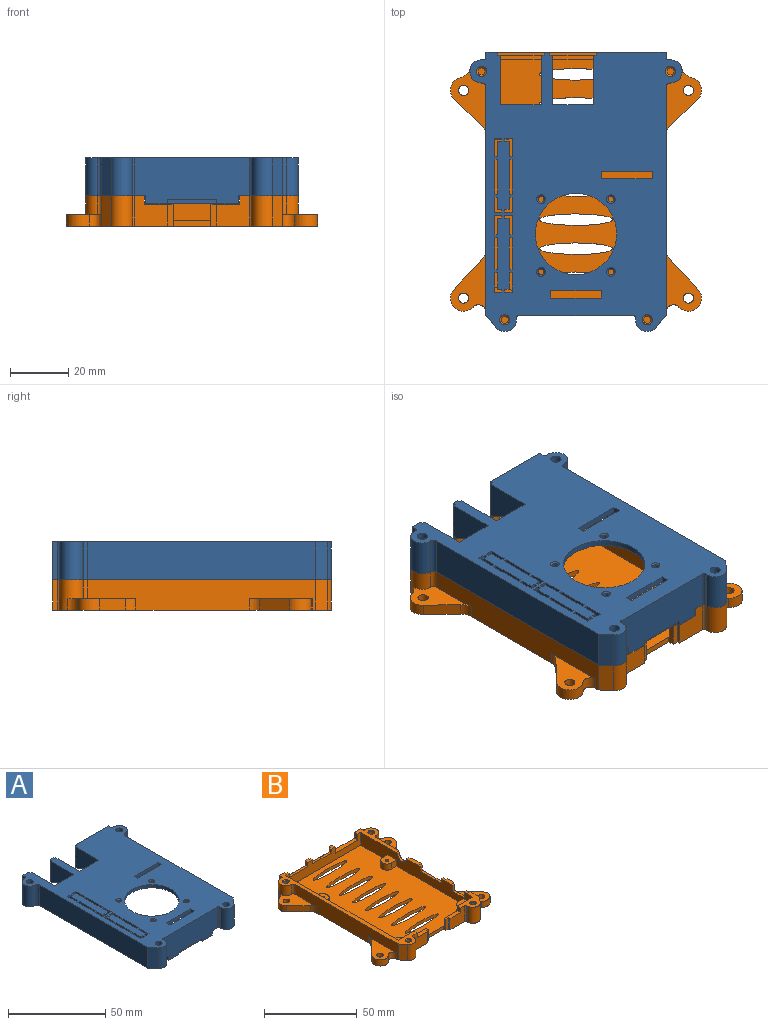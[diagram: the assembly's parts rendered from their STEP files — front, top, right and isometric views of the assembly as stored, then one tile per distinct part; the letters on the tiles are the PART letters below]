
ASSEMBLY  parts=2 mates=1
PART A: 159 faces, bbox 73x96x15.8 mm
  f0: plane 32x2.5mm, normal (0,0,-1), area 63mm2, adj f67,f68,f153,f154,f155,f156,f157
  f1: plane 96x20.5mm, normal (0,0,-1), area 322.4mm2, adj f67,f68,f69,f70,f71,f72,f73,f74
  f2: plane 30.5x10.5mm, normal (0,0,-1), area 109.1mm2, adj f3,f4,f65,f90,f91,f92,f93,f94
  f3: plane 78.5x13mm, normal (1,0,0), area 841.2mm2, adj f2,f5,f6,f52,f85,f89,f90,f140
  f4: plane 85.5x11mm, normal (-1,0,0), area 848.3mm2, adj f2,f5,f6,f7,f68,f85,f96,f136
  f5: plane 10.5x2.5mm, normal (0,0,-1), area 22.8mm2, adj f3,f4,f144,f146,f147,f150,f151,f152
  f6: plane 8.5x2.5mm, normal (0,0,-1), area 17.8mm2, adj f3,f4,f137,f139,f140,f143,f146,f148
  f7: plane 85.5x57mm, normal (0,0,-1), area 2695.7mm2, adj f4,f53,f59,f63,f64,f68,f69,f70
  f8: plane 12x1.2mm, normal (1,0,0), area 14.4mm2, adj f9,f10,f52,f134
  f9: plane 1.2x1mm, normal (0,-1,0), area 1.2mm2, adj f8,f52,f125,f134
  f10: plane 1.2x1mm, normal (0,1,0), area 1.2mm2, adj f8,f52,f125,f134
  f11: plane 1.2x1mm, normal (0,-1,0), area 1.2mm2, adj f13,f52,f123,f134
  f12: plane 1.2x1mm, normal (0,1,0), area 1.2mm2, adj f13,f52,f123,f134
  f13: plane 12x1.2mm, normal (-1,0,0), area 14.4mm2, adj f11,f12,f52,f134
  f14: plane 1.2x1mm, normal (-1,0,0), area 1.2mm2, adj f16,f52,f106,f134
  f15: plane 1.2x1mm, normal (0,-1,0), area 1.2mm2, adj f17,f52,f123,f134
  f16: plane 1.5x1.2mm, normal (0,-1,0), area 1.8mm2, adj f14,f17,f52,f134
  f17: plane 4.25x1.2mm, normal (-1,0,0), area 5.1mm2, adj f15,f16,f52,f134
  f18: plane 1.2x1mm, normal (0,-1,0), area 1.2mm2, adj f20,f52,f125,f134
  f19: plane 1.2x1mm, normal (1,0,0), area 1.2mm2, adj f21,f52,f106,f134
  f20: plane 4.25x1.2mm, normal (1,0,0), area 5.1mm2, adj f18,f21,f52,f134
  f21: plane 1.5x1.2mm, normal (0,-1,0), area 1.8mm2, adj f19,f20,f52,f134
  f22: plane 1.2x1mm, normal (1,0,0), area 1.2mm2, adj f23,f52,f107,f135
  f23: plane 1.5x1.2mm, normal (0,1,0), area 1.8mm2, adj f22,f24,f52,f135
  f24: plane 5.75x1.2mm, normal (1,0,0), area 6.9mm2, adj f23,f25,f52,f135
  f25: plane 1.2x1mm, normal (0,1,0), area 1.2mm2, adj f24,f52,f122,f135
  f26: plane 1.2x1mm, normal (0,1,0), area 1.2mm2, adj f27,f52,f120,f135
  f27: plane 5.75x1.2mm, normal (-1,0,0), area 6.9mm2, adj f26,f28,f52,f135
  f28: plane 1.5x1.2mm, normal (0,1,0), area 1.8mm2, adj f27,f29,f52,f135
  f29: plane 1.2x1mm, normal (-1,0,0), area 1.2mm2, adj f28,f52,f107,f135
  f30: plane 1.2x1mm, normal (0,-1,0), area 1.2mm2, adj f32,f52,f120,f135
  f31: plane 1.2x1mm, normal (0,1,0), area 1.2mm2, adj f32,f52,f120,f135
  f32: plane 11x1.2mm, normal (-1,0,0), area 13.2mm2, adj f30,f31,f52,f135
  f33: plane 1.2x1mm, normal (0,-1,0), area 1.2mm2, adj f34,f52,f122,f135
  f34: plane 11x1.2mm, normal (1,0,0), area 13.2mm2, adj f33,f35,f52,f135
  f35: plane 1.2x1mm, normal (0,1,0), area 1.2mm2, adj f34,f52,f122,f135
  f36: plane 1.2x1mm, normal (-1,0,0), area 1.2mm2, adj f37,f52,f121,f135
  f37: plane 1.5x1.2mm, normal (0,-1,0), area 1.8mm2, adj f36,f38,f52,f135
  f38: plane 5.75x1.2mm, normal (-1,0,0), area 6.9mm2, adj f37,f39,f52,f135
  f39: plane 1.2x1mm, normal (0,-1,0), area 1.2mm2, adj f38,f52,f120,f135
  f40: plane 1.2x1mm, normal (0,-1,0), area 1.2mm2, adj f42,f52,f122,f135
  f41: plane 1.2x1mm, normal (1,0,0), area 1.2mm2, adj f43,f52,f121,f135
  f42: plane 5.75x1.2mm, normal (1,0,0), area 6.9mm2, adj f40,f43,f52,f135
  f43: plane 1.5x1.2mm, normal (0,-1,0), area 1.8mm2, adj f41,f42,f52,f135
  f44: plane 1.2x1mm, normal (0,1,0), area 1.2mm2, adj f45,f52,f123,f134
  f45: plane 5.25x1.2mm, normal (-1,0,0), area 6.3mm2, adj f44,f46,f52,f134
  f46: plane 1.5x1.2mm, normal (0,1,0), area 1.8mm2, adj f45,f47,f52,f134
  f47: plane 1.2x1mm, normal (-1,0,0), area 1.2mm2, adj f46,f52,f124,f134
  f48: plane 1.2x1mm, normal (1,0,0), area 1.2mm2, adj f49,f52,f124,f134
  f49: plane 1.5x1.2mm, normal (0,1,0), area 1.8mm2, adj f48,f50,f52,f134
  f50: plane 5.25x1.2mm, normal (1,0,0), area 6.3mm2, adj f49,f51,f52,f134
  f51: plane 1.2x1mm, normal (0,1,0), area 1.2mm2, adj f50,f52,f125,f134
  f52: plane 96x73mm, normal (0,0,1), area 4382.9mm2, adj f3,f8,f9,f10,f11,f12,f13,f14
  f53: plane 32x13mm, normal (1,0,0), area 186.2mm2, adj f7,f52,f54,f60,f97,f99,f103,f104
  f54: plane 13x1mm, normal (0,1,0), area 13mm2, adj f52,f53,f55,f60
  f55: plane 13x1mm, normal (1,0,0), area 13mm2, adj f52,f54,f56,f60
  f56: plane 13x2mm, normal (0,1,0), area 26mm2, adj f52,f55,f57,f60
  f57: plane 13x1mm, normal (-1,0,0), area 13mm2, adj f52,f56,f58,f60
  f58: plane 13x1mm, normal (0,1,0), area 13mm2, adj f52,f57,f59,f60
  f59: plane 24x13mm, normal (-1,0,0), area 174.3mm2, adj f7,f52,f58,f60,f98,f99
  f60: plane 4x2.5mm, normal (0,0,-1), area 8mm2, adj f53,f54,f55,f56,f57,f58,f59,f99
  f61: plane 13x1mm, normal (-1,0,0), area 13mm2, adj f52,f62,f65,f66
  f62: plane 13x1mm, normal (0,1,0), area 13mm2, adj f52,f61,f63,f66
  f63: plane 32x13mm, normal (-1,0,0), area 186.3mm2, adj f7,f52,f62,f66,f97,f100,f103,f104
  f64: plane 25x11.8mm, normal (1,0,0), area 169.6mm2, adj f7,f65,f66,f100,f101,f102
  f65: plane 24x13mm, normal (0,1,0), area 111.4mm2, adj f2,f52,f61,f64,f66,f94,f95,f102
  f66: plane 3x2.5mm, normal (0,0,-1), area 6.5mm2, adj f61,f62,f63,f64,f65,f100
  f67: plane 39.5x15.8mm, normal (0,-1,0), area 577.6mm2, adj f0,f1,f52,f84,f85,f86,f153,f154
  f68: plane 57x13.8mm, normal (0,1,0), area 716.6mm2, adj f0,f1,f4,f7,f69,f85,f153,f154
  f69: plane 85.5x11mm, normal (1,0,0), area 940.5mm2, adj f1,f7,f68,f70
  f70: plane 11x2.5mm, normal (0,-1,0), area 27.5mm2, adj f1,f7,f69,f71
  f71: plane 17x13mm, normal (1,0,0), area 50.5mm2, adj f1,f7,f52,f70,f72,f98
  f72: plane 13x1mm, normal (0,1,0), area 13mm2, adj f1,f52,f71,f73
  f73: plane 13x1mm, normal (1,0,0), area 13mm2, adj f1,f52,f72,f74
  f74: plane 13x4mm, normal (0,1,0), area 52mm2, adj f1,f52,f73,f75
  f75: plane 13x1.75mm, normal (-1,0,0), area 22.8mm2, adj f1,f52,f74,f76
  f76: cylinder r=0.75mm len=13mm, axis (0,0,-1), area 15.3mm2, adj f1,f52,f75,f77
  f77: plane 13x0.75mm, normal (0,1,0), area 9.7mm2, adj f1,f52,f76,f78
  f78: cylinder r=4mm len=13mm, axis (0,0,-1), area 163.4mm2, adj f1,f52,f77,f79
  f79: cylinder r=1.5mm len=13mm, axis (0,0,-1), area 30.6mm2, adj f1,f52,f78,f80
  f80: plane 78.5x13mm, normal (-1,0,0), area 1020.5mm2, adj f1,f52,f79,f81
  f81: plane 13x4.08mm, normal (-0.76,-0.64,0), area 69.4mm2, adj f1,f52,f80,f82
  f82: cylinder r=4mm len=13mm, axis (0,0,-1), area 126.9mm2, adj f1,f52,f81,f83
  f83: plane 13x0.75mm, normal (1,0,0), area 9.7mm2, adj f1,f52,f82,f84
  f84: cylinder r=0.75mm len=13mm, axis (0,0,-1), area 15.3mm2, adj f1,f52,f67,f83
  f85: plane 15x14.5mm, normal (0,0,-1), area 83.8mm2, adj f3,f4,f67,f68,f86,f87,f88,f89
  f86: cylinder r=0.75mm len=13mm, axis (0,0,-1), area 15.3mm2, adj f52,f67,f85,f87
  f87: plane 13x0.75mm, normal (-1,0,0), area 9.7mm2, adj f52,f85,f86,f88
  f88: cylinder r=4mm len=13mm, axis (0,0,-1), area 126.9mm2, adj f52,f85,f87,f89
  f89: plane 13x4.08mm, normal (0.76,-0.64,0), area 69.4mm2, adj f3,f52,f85,f88
  f90: cylinder r=1.5mm len=13mm, axis (0,0,-1), area 30.6mm2, adj f2,f3,f52,f91
  f91: cylinder r=4mm len=13mm, axis (0,0,-1), area 163.4mm2, adj f2,f52,f90,f92
  f92: plane 13x0.75mm, normal (0,1,0), area 9.8mm2, adj f2,f52,f91,f93
  f93: cylinder r=0.75mm len=13mm, axis (0,0,-1), area 15.3mm2, adj f2,f52,f92,f94
  f94: plane 13x1.75mm, normal (1,0,0), area 22.8mm2, adj f2,f52,f65,f93
  f95: plane 23x11.8mm, normal (-1,0,0), area 45.9mm2, adj f2,f7,f65,f96,f101,f102
  f96: plane 11x2.5mm, normal (0,-1,0), area 27.5mm2, adj f2,f4,f7,f95
  f97: plane 14x1.2mm, normal (0,1,0), area 16.8mm2, adj f52,f53,f63,f104
  f98: plane 14x2mm, normal (0,1,0), area 28mm2, adj f7,f52,f59,f71
  f99: plane 22.5x11mm, normal (0,-0.44,-0.9), area 100.2mm2, adj f7,f53,f59,f60
  f100: plane 22.5x11mm, normal (0,-0.44,-0.9), area 75.1mm2, adj f7,f63,f64,f66
  f101: plane 17x0.8mm, normal (0,1,0), area 13.6mm2, adj f7,f64,f95,f102
  f102: plane 23x17mm, normal (0,0,-1), area 391mm2, adj f64,f65,f95,f101
  f103: plane 14x0.8mm, normal (0,1,0), area 11.2mm2, adj f7,f53,f63,f104
  f104: plane 15x14mm, normal (0,0,-1), area 210mm2, adj f53,f63,f97,f103
  f105: cylinder r=14mm len=28mm, axis (0,0,1), area 175.9mm2, adj f7,f52
  f106: plane 6x2mm, normal (0,1,0), area 10.8mm2, adj f7,f14,f19,f52,f123,f125,f134
  f107: plane 6x2mm, normal (0,-1,0), area 10.8mm2, adj f7,f22,f29,f52,f120,f122,f135
  f108: cylinder r=1mm len=2mm, axis (0,0,1), area 9.4mm2, adj f7,f127
  f109: plane 2.5x2mm, normal (1,0,0), area 5mm2, adj f7,f52,f110,f111
  f110: plane 17.5x2mm, normal (0,-1,0), area 35mm2, adj f7,f52,f109,f112
  f111: plane 17.5x2mm, normal (0,1,0), area 35mm2, adj f7,f52,f109,f112
  f112: plane 2.5x2mm, normal (-1,0,0), area 5mm2, adj f7,f52,f110,f111
  f113: cylinder r=1mm len=2mm, axis (0,0,1), area 9.4mm2, adj f7,f126
  f114: cylinder r=1mm len=2mm, axis (0,0,1), area 9.4mm2, adj f7,f129
  f115: cylinder r=1mm len=2mm, axis (0,0,1), area 9.4mm2, adj f7,f128
  f116: plane 2.5x2mm, normal (1,0,0), area 5mm2, adj f7,f52,f117,f118
  f117: plane 17.5x2mm, normal (0,-1,0), area 35mm2, adj f7,f52,f116,f119
  f118: plane 17.5x2mm, normal (0,1,0), area 35mm2, adj f7,f52,f116,f119
  f119: plane 2.5x2mm, normal (-1,0,0), area 5mm2, adj f7,f52,f117,f118
  f120: plane 26.5x2mm, normal (1,0,0), area 50.6mm2, adj f7,f26,f30,f31,f39,f52,f107,f121
  f121: plane 6x2mm, normal (0,1,0), area 10.8mm2, adj f7,f36,f41,f52,f120,f122,f135
  f122: plane 26.5x2mm, normal (-1,0,0), area 50.6mm2, adj f7,f25,f33,f35,f40,f52,f107,f121
  f123: plane 25.5x2mm, normal (1,0,0), area 48.6mm2, adj f7,f11,f12,f15,f44,f52,f106,f124
  f124: plane 6x2mm, normal (0,-1,0), area 10.8mm2, adj f7,f47,f48,f52,f123,f125,f134
  f125: plane 25.5x2mm, normal (-1,0,0), area 48.6mm2, adj f7,f9,f10,f18,f51,f52,f106,f124
  f126: cone r=1mm half-angle=45deg, axis (0,0,1), area 5.6mm2, adj f52,f113
  f127: cone r=1mm half-angle=45deg, axis (0,0,1), area 5.6mm2, adj f52,f108
  f128: cone r=1mm half-angle=45deg, axis (0,0,1), area 5.6mm2, adj f52,f115
  f129: cone r=1mm half-angle=45deg, axis (0,0,1), area 5.6mm2, adj f52,f114
  f130: cylinder r=1.75mm len=13mm, axis (0,0,1), area 142.9mm2, adj f1,f52
  f131: cylinder r=1.75mm len=13mm, axis (0,0,1), area 142.9mm2, adj f52,f85
  f132: cylinder r=1.75mm len=13mm, axis (0,0,1), area 142.9mm2, adj f2,f52
  f133: cylinder r=1.75mm len=13mm, axis (0,0,1), area 142.9mm2, adj f1,f52
  f134: plane 25.5x6mm, normal (0,0,-1), area 100mm2, adj f8,f9,f10,f11,f12,f13,f14,f15
  f135: plane 26.5x6mm, normal (0,0,-1), area 104mm2, adj f22,f23,f24,f25,f26,f27,f28,f29
  f136: plane 1.5x1mm, normal (0,1,0), area 1.5mm2, adj f4,f85,f138,f139
  f137: plane 1.5x1mm, normal (0,-1,0), area 1.5mm2, adj f4,f6,f138,f139
  f138: plane 9x1.5mm, normal (0,0,-1), area 13.5mm2, adj f4,f136,f137,f139
  f139: plane 12x2.5mm, normal (1,0,0), area 21mm2, adj f6,f85,f136,f137,f138,f140,f141,f142
  f140: plane 2.5x1mm, normal (0,-1,0), area 2.5mm2, adj f3,f6,f139,f142
  f141: plane 2.5x1mm, normal (0,1,0), area 2.5mm2, adj f3,f85,f139,f142
  f142: plane 12x1mm, normal (0,0,-1), area 12mm2, adj f3,f139,f140,f141
  f143: plane 4x1.5mm, normal (0,1,0), area 6mm2, adj f4,f6,f145,f146
  f144: plane 4x1.5mm, normal (0,-1,0), area 6mm2, adj f4,f5,f145,f146
  f145: plane 16x1.5mm, normal (0,0,-1), area 24mm2, adj f4,f143,f144,f146
  f146: plane 20x5.5mm, normal (1,0,0), area 46mm2, adj f5,f6,f143,f144,f145,f147,f148,f149
  f147: plane 5.5x1mm, normal (0,-1,0), area 5.5mm2, adj f3,f5,f146,f149
  f148: plane 5.5x1mm, normal (0,1,0), area 5.5mm2, adj f3,f6,f146,f149
  f149: plane 20x1mm, normal (0,0,-1), area 20mm2, adj f3,f146,f147,f148
  f150: cylinder r=3.5mm len=7mm, axis (1,0,0), area 16.5mm2, adj f2,f4,f5,f152
  f151: cylinder r=5mm len=10mm, axis (1,0,0), area 15.7mm2, adj f2,f3,f5,f152
  f152: plane 10x5mm, normal (1,0,0), area 20mm2, adj f2,f5,f150,f151
  f153: plane 2.8x2.5mm, normal (-1,0,0), area 7mm2, adj f0,f1,f67,f68
  f154: plane 2.8x2.5mm, normal (1,0,0), area 7mm2, adj f0,f67,f68,f85
  f155: plane 1.5x1mm, normal (1,0,0), area 1.5mm2, adj f0,f67,f156,f158
  f156: plane 17x1.5mm, normal (0,-1,0), area 25.5mm2, adj f0,f155,f157,f158
  f157: plane 1.5x1mm, normal (-1,0,0), area 1.5mm2, adj f0,f67,f156,f158
  f158: plane 17x1mm, normal (0,0,-1), area 17mm2, adj f67,f155,f156,f157
PART B: 150 faces, bbox 86.4x96x10.5 mm
  f0: cylinder r=1.25mm len=7mm, axis (0,0,-1), area 55mm2, adj f145,f146
  f1: cylinder r=1.25mm len=7mm, axis (0,0,-1), area 55mm2, adj f144,f147
  f2: cylinder r=1.25mm len=7mm, axis (0,0,-1), area 55mm2, adj f143,f148
  f3: cylinder r=1.25mm len=7mm, axis (0,0,-1), area 55mm2, adj f142,f149
  f4: plane 78.5x10.5mm, normal (1,0,0), area 466.2mm2, adj f10,f11,f21,f22,f23,f68,f69,f70
  f5: plane 78.5x10.5mm, normal (-1,0,0), area 671.5mm2, adj f10,f14,f97,f105,f117,f121,f122,f125
  f6: plane 11.25x10.5mm, normal (0,-1,0), area 94.1mm2, adj f10,f11,f88,f89,f92,f99
  f7: plane 11.25x10.5mm, normal (0,-1,0), area 94.1mm2, adj f10,f14,f86,f87,f91,f94
  f8: plane 7.5x2mm, normal (-1,0,0), area 12.2mm2, adj f10,f33,f35,f39,f88,f93
  f9: plane 7.5x2mm, normal (1,0,0), area 12.2mm2, adj f10,f12,f35,f39,f86,f90
  f10: plane 96x86.39mm, normal (0,0,-1), area 5621.8mm2, adj f4,f5,f6,f7,f8,f9,f24,f35
  f11: plane 14.5x14.5mm, normal (0,0,1), area 82.6mm2, adj f4,f6,f28,f32,f33,f68,f71,f89
  f12: plane 22x8.5mm, normal (0,1,0), area 127mm2, adj f9,f14,f34,f39,f47,f50,f86,f87
  f13: plane 4x2.5mm, normal (0,0,1), area 8mm2, adj f15,f20,f36,f38,f80,f81,f82,f85
  f14: plane 96x20mm, normal (0,0,1), area 321.2mm2, adj f5,f7,f12,f17,f34,f36,f37,f38
  f15: plane 2.5x1.5mm, normal (-1,0,0), area 3.8mm2, adj f13,f16,f38,f85
  f16: plane 14x1.5mm, normal (0,0,1), area 21mm2, adj f15,f17,f38,f85
  f17: plane 2.5x1.5mm, normal (1,0,0), area 3.8mm2, adj f14,f16,f38,f85
  f18: plane 2.5x1.5mm, normal (-1,0,0), area 3.8mm2, adj f19,f31,f38,f81
  f19: plane 14x1.5mm, normal (0,0,1), area 21mm2, adj f18,f20,f38,f81
  f20: plane 2.5x1.5mm, normal (1,0,0), area 3.8mm2, adj f13,f19,f38,f81
  f21: plane 8.5x2.5mm, normal (0,0,1), area 17.8mm2, adj f4,f25,f30,f32,f70,f71,f72,f75
  f22: plane 10.5x2.5mm, normal (0,0,1), area 22.8mm2, adj f4,f27,f32,f64,f74,f75,f76,f77
  f23: plane 30.5x10.5mm, normal (0,0,1), area 109.1mm2, adj f4,f24,f32,f36,f38,f64,f65,f76
  f24: plane 10.5x1.75mm, normal (1,0,0), area 18.4mm2, adj f10,f23,f36,f108
  f25: plane 3x1.5mm, normal (0,1,0), area 4.5mm2, adj f21,f26,f32,f75
  f26: plane 16x1.5mm, normal (0,0,1), area 24mm2, adj f25,f27,f32,f75
  f27: plane 3x1.5mm, normal (0,-1,0), area 4.5mm2, adj f22,f26,f32,f75
  f28: plane 4x1.5mm, normal (0,1,0), area 6mm2, adj f11,f29,f32,f71
  f29: plane 9x1.5mm, normal (0,0,1), area 13.5mm2, adj f28,f30,f32,f71
  f30: plane 4x1.5mm, normal (0,-1,0), area 6mm2, adj f21,f29,f32,f71
  f31: plane 3x2.5mm, normal (0,0,1), area 6.5mm2, adj f18,f36,f38,f67,f78,f81
  f32: plane 85.5x8.5mm, normal (-1,0,0), area 567.5mm2, adj f11,f21,f22,f23,f25,f26,f27,f28
  f33: plane 22x8.5mm, normal (0,1,0), area 127mm2, adj f8,f11,f32,f39,f54,f56,f88,f89
  f34: plane 85.5x8.5mm, normal (1,0,0), area 670.8mm2, adj f12,f14,f38,f39,f40,f43,f44,f46
  f35: plane 13x2mm, normal (0,-1,0), area 26mm2, adj f8,f9,f10,f39
  f36: plane 62x10.5mm, normal (0,1,0), area 471mm2, adj f10,f13,f14,f23,f24,f31,f37,f65
  f37: plane 10.5x1.75mm, normal (-1,0,0), area 18.4mm2, adj f10,f14,f36,f104
  f38: plane 57x8.5mm, normal (0,-1,0), area 346.5mm2, adj f13,f14,f15,f16,f17,f18,f19,f20
  f39: plane 85.5x57mm, normal (0,0,1), area 4044.5mm2, adj f8,f9,f12,f32,f33,f34,f35,f38
  f40: plane 4x4mm, normal (0,-1,0), area 16mm2, adj f34,f39,f41,f44
  f41: cylinder r=3.5mm len=7mm, axis (0,0,-1), area 44mm2, adj f39,f40,f43,f44
  f42: cylinder r=1mm len=4mm, axis (0,0,-1), area 25.1mm2, adj f44,f45
  f43: plane 4x4mm, normal (0,1,0), area 16mm2, adj f34,f39,f41,f44
  f44: plane 7.5x7mm, normal (0,0,1), area 44.1mm2, adj f34,f40,f41,f42,f43
  f45: plane 2x2mm, normal (0,0,1), area 3.1mm2, adj f42
  f46: plane 4x4mm, normal (0,1,0), area 16mm2, adj f34,f39,f48,f50
  f47: plane 4x3.5mm, normal (1,0,0), area 14mm2, adj f12,f39,f48,f50
  f48: cylinder r=3.5mm len=4mm, axis (0,0,-1), area 22mm2, adj f39,f46,f47,f50
  f49: cylinder r=1mm len=4mm, axis (0,0,-1), area 25.1mm2, adj f50,f51
  f50: plane 7.5x7mm, normal (0,0,1), area 46.7mm2, adj f12,f34,f46,f47,f48,f49
  f51: plane 2x2mm, normal (0,0,1), area 3.1mm2, adj f49
  f52: plane 4x4mm, normal (0,1,0), area 16mm2, adj f32,f39,f53,f56
  f53: cylinder r=3.5mm len=4mm, axis (0,0,-1), area 22mm2, adj f39,f52,f54,f56
  f54: plane 4x3.5mm, normal (-1,0,0), area 14mm2, adj f33,f39,f53,f56
  f55: cylinder r=1mm len=4mm, axis (0,0,-1), area 25.1mm2, adj f56,f57
  f56: plane 7.5x7mm, normal (0,0,1), area 46.7mm2, adj f32,f33,f52,f53,f54,f55
  f57: plane 2x2mm, normal (0,0,1), area 3.1mm2, adj f55
  f58: plane 4x4mm, normal (0,1,0), area 16mm2, adj f32,f39,f59,f62
  f59: cylinder r=3.5mm len=7mm, axis (0,0,-1), area 44mm2, adj f39,f58,f61,f62
  f60: cylinder r=1mm len=4mm, axis (0,0,-1), area 25.1mm2, adj f62,f63
  f61: plane 4x4mm, normal (0,-1,0), area 16mm2, adj f32,f39,f59,f62
  f62: plane 7.5x7mm, normal (0,0,1), area 44.1mm2, adj f32,f58,f59,f60,f61
  f63: plane 2x2mm, normal (0,0,1), area 3.1mm2, adj f60
  f64: cylinder r=3.5mm len=7mm, axis (1,0,0), area 16.5mm2, adj f22,f23,f32,f77
  f65: plane 4x2.5mm, normal (-1,0,0), area 10mm2, adj f23,f36,f38,f66
  f66: plane 17x2.5mm, normal (0,0,1), area 42.5mm2, adj f36,f38,f65,f67
  f67: plane 4x2.5mm, normal (1,0,0), area 10mm2, adj f31,f36,f38,f66
  f68: plane 5.5x1mm, normal (0,1,0), area 5.5mm2, adj f4,f11,f69,f71
  f69: plane 12x1mm, normal (0,0,1), area 12mm2, adj f4,f68,f70,f71
  f70: plane 5.5x1mm, normal (0,-1,0), area 5.5mm2, adj f4,f21,f69,f71
  f71: plane 12x5.5mm, normal (1,0,0), area 30mm2, adj f11,f21,f28,f29,f30,f68,f69,f70
  f72: plane 5x1mm, normal (0,1,0), area 5mm2, adj f4,f21,f73,f75
  f73: plane 20x1mm, normal (0,0,1), area 20mm2, adj f4,f72,f74,f75
  f74: plane 5x1mm, normal (0,-1,0), area 5mm2, adj f4,f22,f73,f75
  f75: plane 20x5mm, normal (1,0,0), area 52mm2, adj f21,f22,f25,f26,f27,f72,f73,f74
  f76: cylinder r=5mm len=10mm, axis (1,0,0), area 15.7mm2, adj f4,f22,f23,f77
  f77: plane 10x5mm, normal (1,0,0), area 20mm2, adj f22,f23,f64,f76
  f78: plane 3.5x1mm, normal (-1,0,0), area 3.5mm2, adj f31,f36,f79,f81
  f79: plane 16x1mm, normal (0,0,1), area 16mm2, adj f36,f78,f80,f81
  f80: plane 3.5x1mm, normal (1,0,0), area 3.5mm2, adj f13,f36,f79,f81
  f81: plane 16x3.5mm, normal (0,1,0), area 21mm2, adj f13,f18,f19,f20,f31,f78,f79,f80
  f82: plane 3.5x1mm, normal (-1,0,0), area 3.5mm2, adj f13,f36,f83,f85
  f83: plane 16x1mm, normal (0,0,1), area 16mm2, adj f36,f82,f84,f85
  f84: plane 3.5x1mm, normal (1,0,0), area 3.5mm2, adj f14,f36,f83,f85
  f85: plane 16x3.5mm, normal (0,1,0), area 21mm2, adj f13,f14,f15,f16,f17,f82,f83,f84
  f86: plane 10x2.5mm, normal (0,0,1), area 23mm2, adj f7,f9,f12,f87,f90,f91
  f87: plane 3x2.5mm, normal (1,0,0), area 7.5mm2, adj f7,f12,f14,f86
  f88: plane 10x2.5mm, normal (0,0,1), area 23mm2, adj f6,f8,f33,f89,f92,f93
  f89: plane 3x2.5mm, normal (-1,0,0), area 7.5mm2, adj f6,f11,f33,f88
  f90: plane 7.5x2mm, normal (0,-1,0), area 15mm2, adj f9,f10,f86,f91
  f91: plane 7.5x1mm, normal (1,0,0), area 7.5mm2, adj f7,f10,f86,f90
  f92: plane 7.5x1mm, normal (-1,0,0), area 7.5mm2, adj f6,f10,f88,f93
  f93: plane 7.5x2mm, normal (0,-1,0), area 15mm2, adj f8,f10,f88,f92
  f94: cylinder r=0.75mm len=10.5mm, axis (0,0,-1), area 12.4mm2, adj f7,f10,f14,f95
  f95: plane 10.5x0.75mm, normal (1,0,0), area 7.9mm2, adj f10,f14,f94,f96
  f96: cylinder r=4mm len=10.5mm, axis (0,0,-1), area 102.5mm2, adj f10,f14,f95,f97
  f97: plane 10.5x4.08mm, normal (-0.76,-0.64,0), area 56.1mm2, adj f5,f10,f14,f96
  f98: plane 10.5x0.75mm, normal (-1,0,0), area 7.9mm2, adj f10,f11,f99,f101
  f99: cylinder r=0.75mm len=10.5mm, axis (0,0,-1), area 12.4mm2, adj f6,f10,f11,f98
  f100: plane 10.5x4.08mm, normal (0.76,-0.64,0), area 56.1mm2, adj f4,f10,f11,f101
  f101: cylinder r=4mm len=10.5mm, axis (0,0,-1), area 102.5mm2, adj f10,f11,f98,f100
  f102: cylinder r=4mm len=10.5mm, axis (0,0,-1), area 102mm2, adj f10,f14,f103,f105,f116,f121
  f103: plane 10.5x0.75mm, normal (0,1,0), area 7.9mm2, adj f10,f14,f102,f104
  f104: cylinder r=0.75mm len=10.5mm, axis (0,0,-1), area 12.4mm2, adj f10,f14,f37,f103
  f105: cylinder r=1.5mm len=6.5mm, axis (0,0,-1), area 15.3mm2, adj f5,f14,f102,f121
  f106: cylinder r=4mm len=10.5mm, axis (0,0,-1), area 102mm2, adj f10,f23,f107,f109,f110,f115
  f107: cylinder r=1.5mm len=6.5mm, axis (0,0,-1), area 15.3mm2, adj f4,f23,f106,f115
  f108: cylinder r=0.75mm len=10.5mm, axis (0,0,-1), area 12.4mm2, adj f10,f23,f24,f109
  f109: plane 10.5x0.75mm, normal (0,1,0), area 7.9mm2, adj f10,f23,f106,f108
  f110: cylinder r=5mm len=4mm, axis (0,0,-1), area 20.3mm2, adj f10,f106,f111,f115
  f111: cylinder r=4.5mm len=7.62mm, axis (0,0,-1), area 38.3mm2, adj f10,f110,f112,f115
  f112: plane 9.24x8.76mm, normal (0.69,-0.73,0), area 50.9mm2, adj f10,f111,f113,f115
  f113: cylinder r=5mm len=4mm, axis (0,0,-1), area 16.2mm2, adj f4,f10,f112,f115
  f114: cylinder r=1.75mm len=4mm, axis (0,0,-1), area 44mm2, adj f10,f115
  f115: plane 23.37x12.2mm, normal (0,0,1), area 130.1mm2, adj f4,f106,f107,f110,f111,f112,f113,f114
  f116: cylinder r=5mm len=4mm, axis (0,0,-1), area 20.3mm2, adj f10,f102,f120,f121
  f117: cylinder r=5mm len=4mm, axis (0,0,-1), area 16.2mm2, adj f5,f10,f118,f121
  f118: plane 9.24x8.76mm, normal (-0.69,-0.73,0), area 50.9mm2, adj f10,f117,f120,f121
  f119: cylinder r=1.75mm len=4mm, axis (0,0,-1), area 44mm2, adj f10,f121
  f120: cylinder r=4.5mm len=7.62mm, axis (0,0,-1), area 38.3mm2, adj f10,f116,f118,f121
  f121: plane 23.37x12.2mm, normal (0,0,1), area 130.1mm2, adj f5,f102,f105,f116,f117,f118,f119,f120
  f122: cylinder r=2.57mm len=4.43mm, axis (0,0,-1), area 24.5mm2, adj f5,f10,f123,f127
  f123: cylinder r=4.5mm len=7.76mm, axis (0,0,-1), area 56.5mm2, adj f10,f122,f124,f127
  f124: plane 10.1x9.59mm, normal (-0.73,0.69,0), area 55.7mm2, adj f10,f123,f125,f127
  f125: cylinder r=5mm len=4mm, axis (0,0,-1), area 15.2mm2, adj f5,f10,f124,f127
  f126: cylinder r=1.75mm len=4mm, axis (0,0,-1), area 44mm2, adj f10,f127
  f127: plane 21.51x12.2mm, normal (0,0,1), area 132mm2, adj f5,f122,f123,f124,f125,f126
  f128: plane 10.1x9.59mm, normal (0.73,0.69,0), area 55.7mm2, adj f10,f129,f131,f133
  f129: cylinder r=4.5mm len=7.76mm, axis (0,0,-1), area 56.5mm2, adj f10,f128,f130,f133
  f130: cylinder r=2.57mm len=4.43mm, axis (0,0,-1), area 24.5mm2, adj f4,f10,f129,f133
  f131: cylinder r=5mm len=4mm, axis (0,0,-1), area 15.2mm2, adj f4,f10,f128,f133
  f132: cylinder r=1.75mm len=4mm, axis (0,0,-1), area 44mm2, adj f10,f133
  f133: plane 21.51x12.2mm, normal (0,0,1), area 132mm2, adj f4,f128,f129,f130,f131,f132
  f134: extruded ~25x4mm, area 103.7mm2, adj f10,f39
  f135: extruded ~25x4mm, area 103.7mm2, adj f10,f39
  f136: extruded ~25x4mm, area 103.7mm2, adj f10,f39
  f137: extruded ~25x4mm, area 103.7mm2, adj f10,f39
  f138: extruded ~25x4mm, area 103.7mm2, adj f10,f39
  f139: extruded ~25x4mm, area 103.7mm2, adj f10,f39
  f140: extruded ~25x4mm, area 103.7mm2, adj f10,f39
  f141: extruded ~25x4mm, area 103.7mm2, adj f10,f39
  f142: plane 2.5x2.5mm, normal (0,0,1), area 4.9mm2, adj f3
  f143: plane 2.5x2.5mm, normal (0,0,1), area 4.9mm2, adj f2
  f144: plane 2.5x2.5mm, normal (0,0,1), area 4.9mm2, adj f1
  f145: plane 2.5x2.5mm, normal (0,0,1), area 4.9mm2, adj f0
  f146: cone r=1.75mm half-angle=45deg, axis (0,0,1), area 6.7mm2, adj f0,f23
  f147: cone r=1.75mm half-angle=45deg, axis (0,0,1), area 6.7mm2, adj f1,f14
  f148: cone r=1.75mm half-angle=45deg, axis (0,0,1), area 6.7mm2, adj f2,f11
  f149: cone r=1.75mm half-angle=45deg, axis (0,0,1), area 6.7mm2, adj f3,f14
PLACE A t=(-30.84,-28.17,-80.53)mm
PLACE B t=(-30.84,-28.17,19.47)mm
MATE fastened A.f88 <-> B.f2  axis (0,0,-1) through (24.66,-29.67,29.97)mm
